# Revit family: Ginko 1.0
name_source: partatom
category: Lighting Fixtures
revit_build: Autodesk Revit 2017 (Build: 20160225_1515(x64)
units: mm (PartAtom-declared; Revit-internal decimal feet)

## family parameters
Always vertical = No
Cut with Voids When Loaded = No
Light Source = No
OmniClass Number = 23.80.70.00
OmniClass Title = Lighting
Part Type = Normal
Room Calculation Point = No
Round Connector Dimension = Use Diameter
Shared = No
Work Plane-Based = No

## types (7) — shared parameters
Apparent Load Phase 1 = 4 W
Base bracket = Ginko1.0_Base bracket
Bracket = L&L_Stainless steel
Code = GN100 I Stainless steel; GN100 E White; GN100 N Black anodized; GN100 F Grey; GN100 H Anthracite; GN100 T Cor-ten; GN100 5 Jasper green
Control system = -
Cutout dimensions = -
Delivered lumen output = 146 lm (3000K, 19°, 2.5W, CRI 80); 124 lm (3000K, 19°, 2.5W, CRI 90); 193 lm (3000K, 19°, 3.5W, CRI 80); 164 lm (3000K, 19°, 3.5W, CRI 90)
Description = Outdoor projectors
Energy efficiency class = A A+ A++
Features = -
Geometry = Ginko1.0_mod : Ginko_1.0
H1 = 45 mm  [stored 0.147638 ft]
Height mm = 91 mm
IP = 66
Length mm = 49 mm
Lens = L&L_Lens
Lumen output at source = 168 lm (3000K, 2.5W, CRI 80); 147 lm (3000K, 2.5W, CRI 90); 224 lm (3000K, 3.5W, CRI 80); 196 lm (3000K, 3.5W, CRI 90)
Manufacturer = L&L Luce&Light
Material = body in AISI 316L stainless steel or anticorodal aluminium, AISI 316L stainless steel bracket, screen in tempered, transparent extra-clear glass
Middle = L&L_White
Model = Ginko 1.0
Mounting = surface mounted (ceiling, wall, ground, spike)
No. and type of led = 1 power LED, 1/4 ANSI BIN; 50000h L90 B10 (Ta 25°)
Notes = -
Power cables = includes 1,5 m neoprene cable, H05RN-F 2x0,75/0,75 Ø6,3 mm
Power supply = 24Vdc
Power supply unit = not included
Top = L&L_White
URL = https://www.lucelight.it
URL Accessories and power supply units = https://www.lucelight.it
URL Catalogue = https://www.lucelight.it
URL DXF = https://www.lucelight.it
URL Description = https://www.lucelight.it
URL General code = https://www.lucelight.it
URL IES Photometric file = https://www.lucelight.it
URL Image = https://www.lucelight.it
URL Technical sheet = https://www.lucelight.it
Vertical rotation max = 190.00°
Voltage = 24 V
Weight kg = 0.13
Width mm = 34 mm
Wiring = -
X1 = 100 mm  [stored 0.328084 ft]

## per-type parameters (varying)
| type | Base | CRI | LED Colour | Light Source | Optics | Power |
| Ginko 1.0_M 36° (3000K 3.5 W 24Vdc) | L&L_White aluminium | 90 (also available: CRI 80 - ref. URL Technical sheet) | 3000K (also available: 2700K and 4000K - ref. URL Technical sheet) | Light Source : M36° | 36° | 3.5W (also available: 2.5W - ref. URL Technical sheet) |
| Ginko 1.0_Q 58° (3000K 3.5W 24Vdc) | L&L_White | 90 (also available: CRI 80 - ref. URL Technical sheet) | 3000K (also available: 2700K and 4000K - ref. URL Technical sheet) | Light Source : Q58° | 58° | 3.5W (also available: 2.5W - ref. URL Technical sheet) |
| Ginko 1.0_S 19° (3000K 3.5W 24Vdc) | L&L_White | 90 (also available: CRI 80 - ref. URL Technical sheet) | 3000K (also available: 2700K and 4000K - ref. URL Technical sheet) | Light Source : S19° | 19° | 3.5W (also available: 2.5W - ref. URL Technical sheet) |
| Ginko 1.0_T 12° (3000K 3.5W 24Vdc) | L&L_White | 90 (also available: CRI 80 - ref. URL Technical sheet) | 3000K (also available: 2700K and 4000K - ref. URL Technical sheet) | Light Source : T12° | 12° | 3.5W (also available: 2.5W - ref. URL Technical sheet) |
| Ginko 1.0_U 38° (3000K 3.5W 24 Vdc) | L&L_White | 90 (also available: CRI 80 - ref. URL Technical sheet) | 3000K (also available: 2700K and 4000K - ref. URL Technical sheet) | Light Source : U38° | 38° | 3.5W (also available: 2.5W - ref. URL technical sheet) |
| Ginko 1.0_W 16°x36° (3000K 3.5W 24Vdc) | L&L_White | 90 (also available: CRI 80 - ref. URL Technical sheet) | 3000K (also available: 2700K and 4000K - ref. URL Technical sheet) | Light Source : W16°x36° | 16°x36° | 3.5W (also available: 2.5W - ref. URL Technical sheet) |
| Ginko 1.0_X 36°x16° (3000K 3.5W 24Vdc) | L&L_White | 90 (also available: CRI 80 - ref. URL Technical sheet) | 3000K (also available: 2700K and 4000K - ref. URL Technical sheet) | Light Source : X36°x16° | 36°x16° | 3.5W (also available: 2.5W - ref. URL Technical sheet) |

note: [stored X ft] marks values corroborated as IEEE doubles in the binary element streams (Revit-internal decimal feet)

## geometry (parser evidence)
native form markers: Blend x4, Sweep x11
no freeform markers — native parametric forms only
